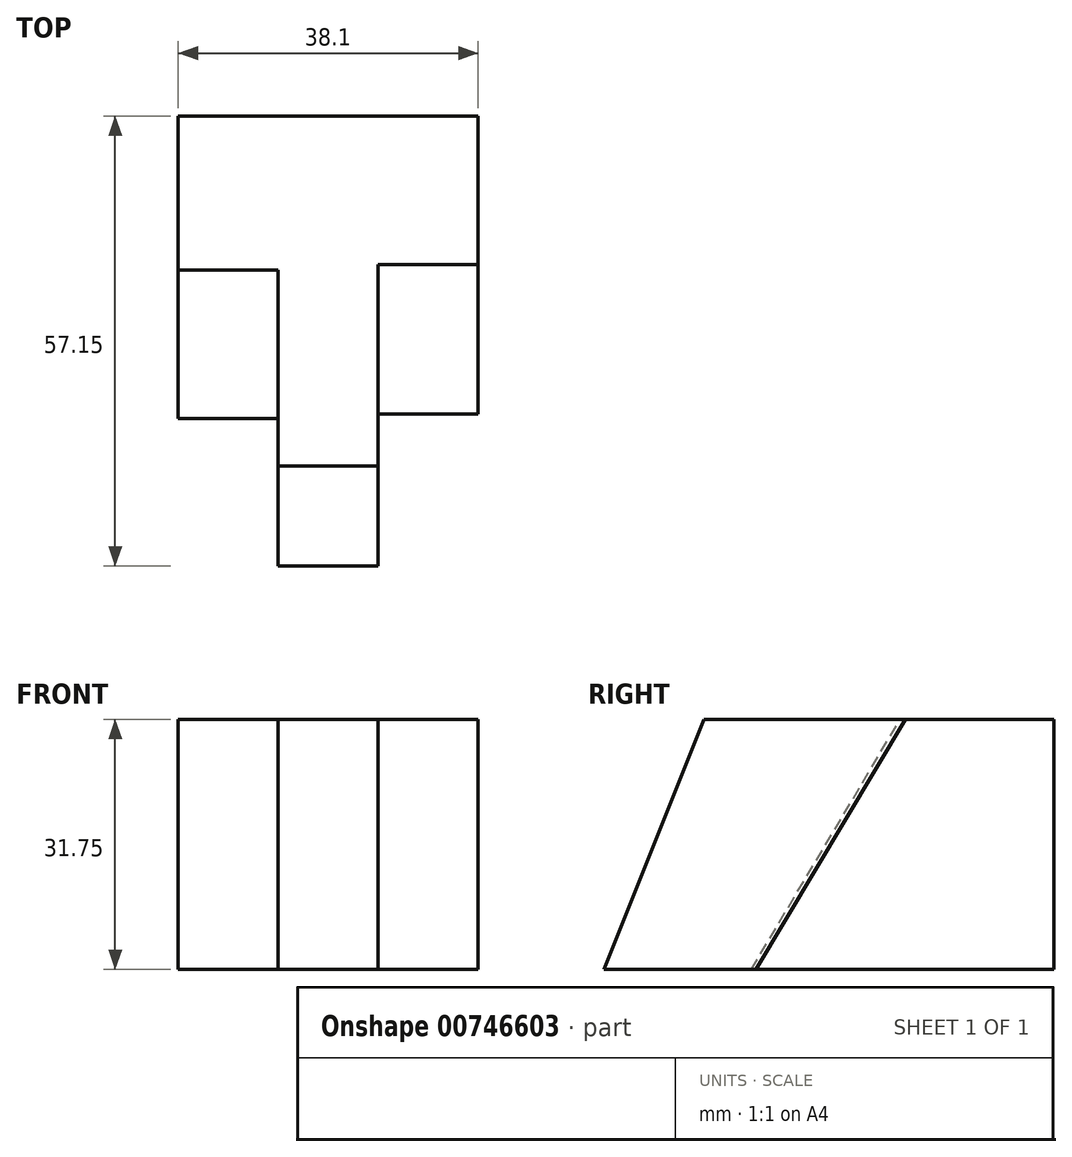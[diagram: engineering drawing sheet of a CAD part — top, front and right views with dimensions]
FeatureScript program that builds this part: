
annotation { "Feature Type Name" : "Feature", "Feature Type Description" : "" }
export const myFeature = defineFeature(function(context is Context, id is Id, definition is map)
    precondition{}
    {
        {
            var Q0;
            Q0=qCreatedBy(makeId("Top.planeOp"),FACE);
            var sketch = newSketch(context, id + "F0", { "sketchPlane" : qUnion([Q0])});
            skLineSegment(sketch, "E0.bottom", {"start": v(0, 0) * mm, "end": v(38.1, 0) * mm});
            skLineSegment(sketch, "E0.top", {"start": v(0, -57.15) * mm, "end": v(38.1, -57.15) * mm});
            skLineSegment(sketch, "E0.left", {"start": v(0, 0) * mm, "end": v(0, -57.15) * mm});
            skLineSegment(sketch, "E0.right", {"start": v(38.1, 0) * mm, "end": v(38.1, -57.15) * mm});
            skSolve(sketch);
        }
        {
            var Q0;
            Q0=makeQuery(id+"F0.imprint","IMPRINT",FACE,{"disambiguationData":[TD([[makeQuery(id+"F0.imprint","IMPRINT",EDGE,{"derivedFrom":sQuery(id+"F0.wireOp",EDGE,"E0.bottom")}),-1.0]])]});
            extrude(context, id + "F1", {"entities" : qUnion([Q0]), "depth" : 31.75 * mm, "offsetDistance" : 25.4 * mm});
        }
        {
            var Q0;
            Q0=makeQuery(id+"F1.opExtrude","SWEPT_FACE",FACE,{"disambiguationData":[OSD([sQuery(id+"F0.wireOp",EDGE,"E0.left")])]});
            var sketch = newSketch(context, id + "F2", { "sketchPlane" : qUnion([Q0])});
            skLineSegment(sketch, "E1", {"start": v(44.45, 31.75) * mm, "end": v(57.15, 0) * mm});
            skLineSegment(sketch, "E2", {"start": v(57.15, 0) * mm, "end": v(57.15, 31.75) * mm});
            skLineSegment(sketch, "E3", {"start": v(57.15, 31.75) * mm, "end": v(44.45, 31.75) * mm});
            skSolve(sketch);
        }
        {
            var Q0;
            Q0 = qSketchRegion(id + "F2", true);
            extrude(context, id + "F3", {"entities" : qUnion([Q0]), "operationType" : NewBodyOperationType.REMOVE, "oppositeDirection" : true, "depth" : 50.8 * mm, "offsetDistance" : 25.4 * mm});
        }
        {
            var Q0;
            Q0=qCreatedBy(makeId("Right.planeOp"),FACE);
            var sketch = newSketch(context, id + "F4", { "sketchPlane" : qUnion([Q0])});
            skLineSegment(sketch, "E4", {"start": v(-19.44, 31.92) * mm, "end": v(-44.97, 31.92) * mm});
            skLineSegment(sketch, "E5", {"start": v(-56.89, 0) * mm, "end": v(-38.44, 0) * mm});
            skLineSegment(sketch, "E6", {"start": v(-38.44, 0) * mm, "end": v(-19.44, 31.92) * mm});
            skLineSegment(sketch, "E7", {"start": v(-44.97, 31.92) * mm, "end": v(-59.16, 0) * mm});
            skLineSegment(sketch, "E8", {"start": v(-59.16, 0) * mm, "end": v(-56.89, 0) * mm});
            skSolve(sketch);
        }
        {
            var Q0;
            Q0=makeQuery(id+"F4.imprint","IMPRINT",FACE,{"disambiguationData":[TD([[makeQuery(id+"F4.imprint","IMPRINT",EDGE,{"derivedFrom":sQuery(id+"F4.wireOp",EDGE,"E4")}),1.0]])]});
            extrude(context, id + "F5", {"entities" : qUnion([Q0]), "operationType" : NewBodyOperationType.REMOVE, "depth" : 12.7 * mm, "offsetDistance" : 25.4 * mm});
        }
        {
            var Q0;
            Q0=makeQuery(id+"F1.opExtrude","SWEPT_FACE",FACE,{"disambiguationData":[OSD([sQuery(id+"F0.wireOp",EDGE,"E0.right")])]});
            var sketch = newSketch(context, id + "F6", { "sketchPlane" : qUnion([Q0])});
            skLineSegment(sketch, "E9", {"start": v(-57.15, 0) * mm, "end": v(-37.88, 0) * mm});
            skLineSegment(sketch, "E10", {"start": v(-37.88, 0) * mm, "end": v(-18.87, 31.75) * mm});
            skLineSegment(sketch, "E11", {"start": v(-18.87, 31.75) * mm, "end": v(-44.45, 31.75) * mm});
            skLineSegment(sketch, "E12", {"start": v(-44.45, 31.75) * mm, "end": v(-57.15, 0) * mm});
            skSolve(sketch);
        }
        {
            var Q0;
            Q0=makeQuery(id+"F6.imprint","IMPRINT",FACE,{"disambiguationData":[TD([[makeQuery(id+"F6.imprint","IMPRINT",EDGE,{"derivedFrom":sQuery(id+"F6.wireOp",EDGE,"E9")}),-1.0]])]});
            extrude(context, id + "F7", {"entities" : qUnion([Q0]), "operationType" : NewBodyOperationType.REMOVE, "oppositeDirection" : true, "depth" : 12.7 * mm, "offsetDistance" : 25.4 * mm});
        }
    });
